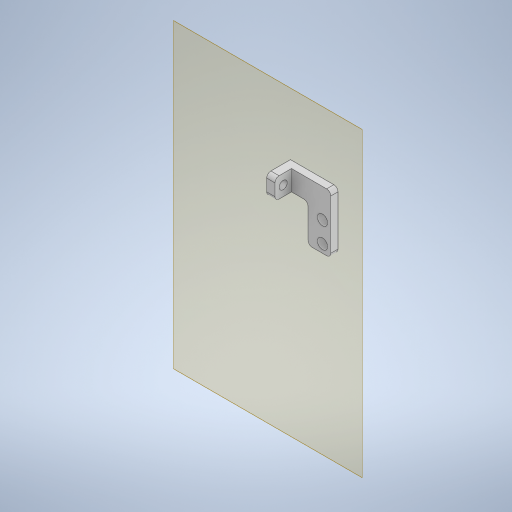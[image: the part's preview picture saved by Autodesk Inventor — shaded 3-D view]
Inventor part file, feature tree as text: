
AUTODESK INVENTOR PART (.ipt)
format: ipt  version: 2024 (Build 280153000, 153)  size: 677,888 bytes
history: native  units: mm
features: other x4, extrude x3, sketch x3, projected_geometry x3, plane x1, fillet x1, reference x1
ambient origin geometry x8: Origin, YZ Plane, XZ Plane, XY Plane, X Axis, Y Axis, Z Axis, Center Point
bodies: Solid1 (feature_tree)
feature tree (16):
  plane  "Work Plane1"
  extrude  "Extrusion1"  Depth=4.0mm
  extrude  "Extrusion3"  Depth=4.0mm
  extrude  "Extrusion5"  Depth=4.0mm
  fillet  "Fillet1"  Radius=0.5mm
  sketch  "Sketch1"  dims[d0=4.0mm d1=4.0mm]
  reference  "Reference1"
  sketch  "Sketch3"  dims[d2=4.0mm d3=7.0mm]
  projected_geometry  "Projected Loop2"
  sketch  "Sketch5"  dims[d4=3.5mm d5=0.0mm d13=0.5mm d14=0.5mm d19=8.0mm d20=0.0mm d26=2.0mm d27=15.0mm d28=4.0mm d29=11.0mm d30=12.0mm d31=90.0deg d32=79.878221mm d33=61.643928mm d34=20.728084mm d35=24.162926mm d36=4.0mm d37=3.9mm d38=7.5mm d39=0.0mm d40=0.0mm]
  projected_geometry  "Projected Loop5"
  projected_geometry  "Projected Loop6"
  other  "<userpath>\Documents\Inventor\robot arm\arms\arms.iam"
  other  "arms.iam"
  other  "lower arm with pulley:1"
  other  "lower arm:1"
